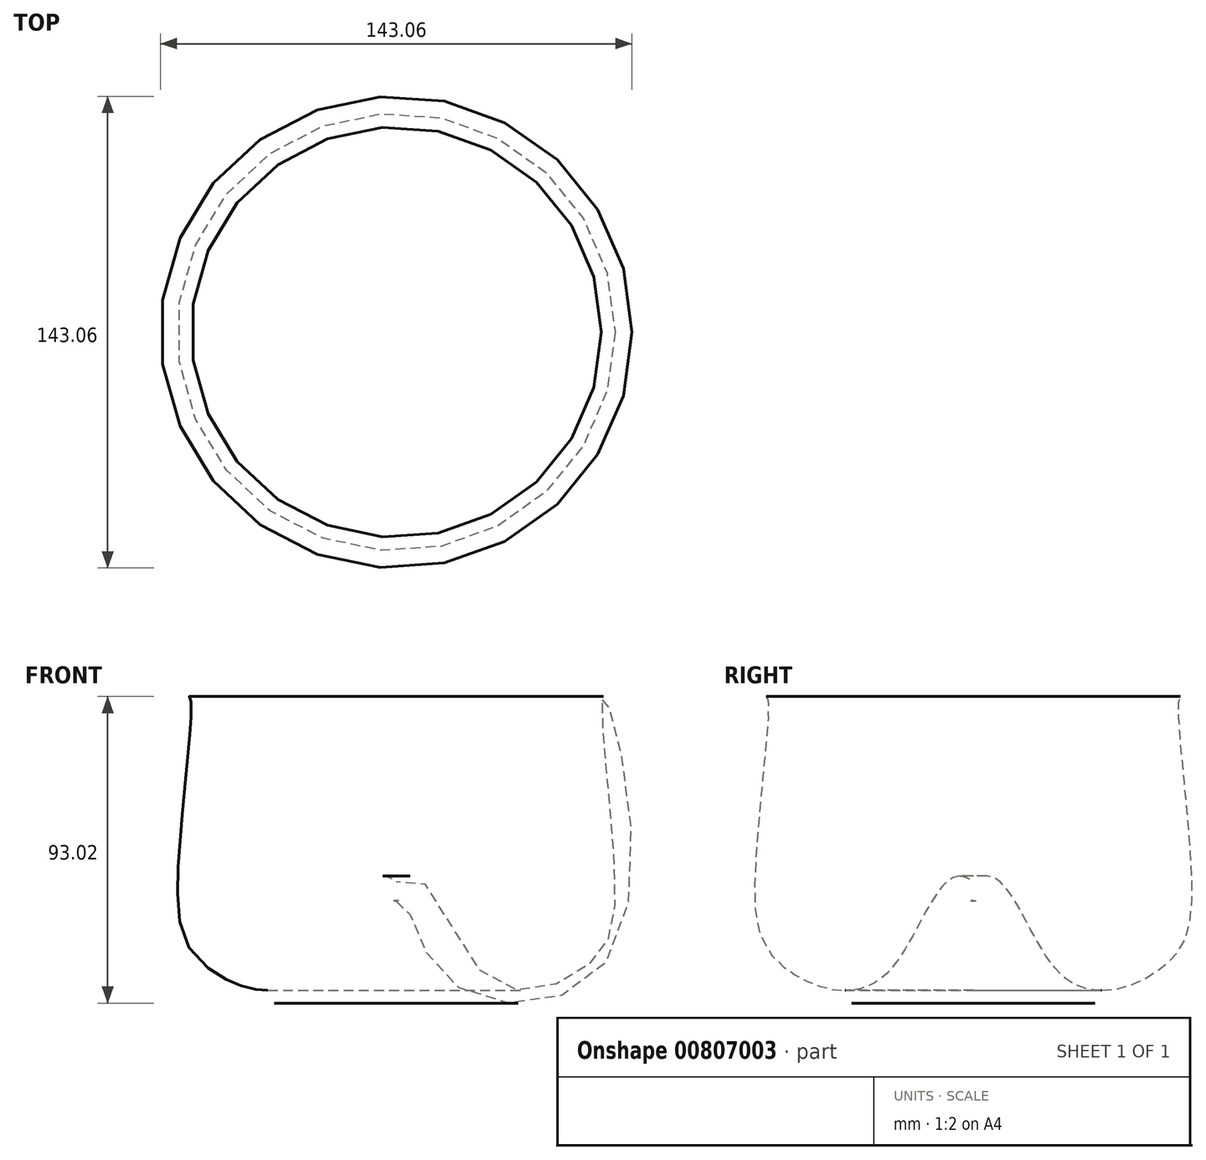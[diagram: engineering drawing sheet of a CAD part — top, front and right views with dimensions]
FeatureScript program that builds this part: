
annotation { "Feature Type Name" : "Feature", "Feature Type Description" : "" }
export const myFeature = defineFeature(function(context is Context, id is Id, definition is map)
    precondition{}
    {
        {
            var Q0;
            Q0=qCreatedBy(makeId("Front.planeOp"),FACE);
            var sketch = newSketch(context, id + "F0", { "sketchPlane" : qUnion([Q0])});
            skFitSpline(sketch, "E0", {"points": [v(0, 0) * mm, v(13.96, -22.3) * mm, v(65.84, -15.04) * mm, v(62.87, 62.08) * mm, v(66.25, 8.22) * mm, v(58.12, -19.43) * mm, v(26.93, -22.53) * mm, v(0, 5.8) * mm], "startDerivative": vector(119.99, 55.38) * mm, "endDerivative": vector(-229.76, -200.37) * mm});
            skFitSpline(sketch, "E1", {"points": [v(0, 5.8) * mm, v(0, 0) * mm], "startDerivative": vector(0, -5.8) * mm, "endDerivative": vector(0, -5.8) * mm});
            skLineSegment(sketch, "E2", {"start": v(0, 23.96) * mm, "end": v(0, -1.4) * mm});
            skSolve(sketch);
        }
        {
            var Q0;
            Q0=makeQuery(id+"F0.imprint","IMPRINT",FACE,{"disambiguationData":[TD([[makeQuery(id+"F0.imprint","IMPRINT",EDGE,{"derivedFrom":sQuery(id+"F0.wireOp",EDGE,"E0")}),1.0]])]});
            var Q1;
            Q1=sQuery(id+"F0.wireOp",EDGE,"E2");
            revolve(context, id + "F1", {"surfaceOperationType" : NewSurfaceOperationType.NEW, "entities" : qUnion([Q0]), "axis" : qUnion([Q1]), "revolveType" : RevolveType.FULL});
        }
        {
            var Q0;
            Q0=qCreatedBy(makeId("Front.planeOp"),FACE);
            var sketch = newSketch(context, id + "F2", { "sketchPlane" : qUnion([Q0])});
            skFitSpline(sketch, "E3", {"points": [v(67.07, 29.09) * mm, v(82.58, 41.06) * mm, v(100.1, 37.95) * mm, v(104.53, 19.78) * mm, v(100.76, 0) * mm, v(78.82, -19.01) * mm, v(50.22, -25) * mm, v(50.44, -25) * mm], "startDerivative": vector(89.8, 97.65) * mm, "endDerivative": vector(21.22, 0.67) * mm});
            skSolve(sketch);
        }
        {
            var Q0;
            Q0=sQuery(id+"F2.wireOp",EDGE,"E3");
            var Q1;
            Q1=sQuery(id+"F2.wireOp",VERTEX,"E3.end");
            cPlane(context, id + "F3", {"entities" : qUnion([Q0, Q1]), "cplaneType" : CPlaneType.CURVE_POINT, "offset" : 25.4 * mm, "width" : 152.4 * mm, "height" : 152.4 * mm});
        }
        {
            var Q0;
            Q0=qCreatedBy(id+"F3.planeOp",FACE);
            var sketch = newSketch(context, id + "F4", { "sketchPlane" : qUnion([Q0])});
            skCircle(sketch, "E4", {"center": v(0, -26.36) * mm, "radius": 1.62 * mm});
            skSolve(sketch);
        }
    });
